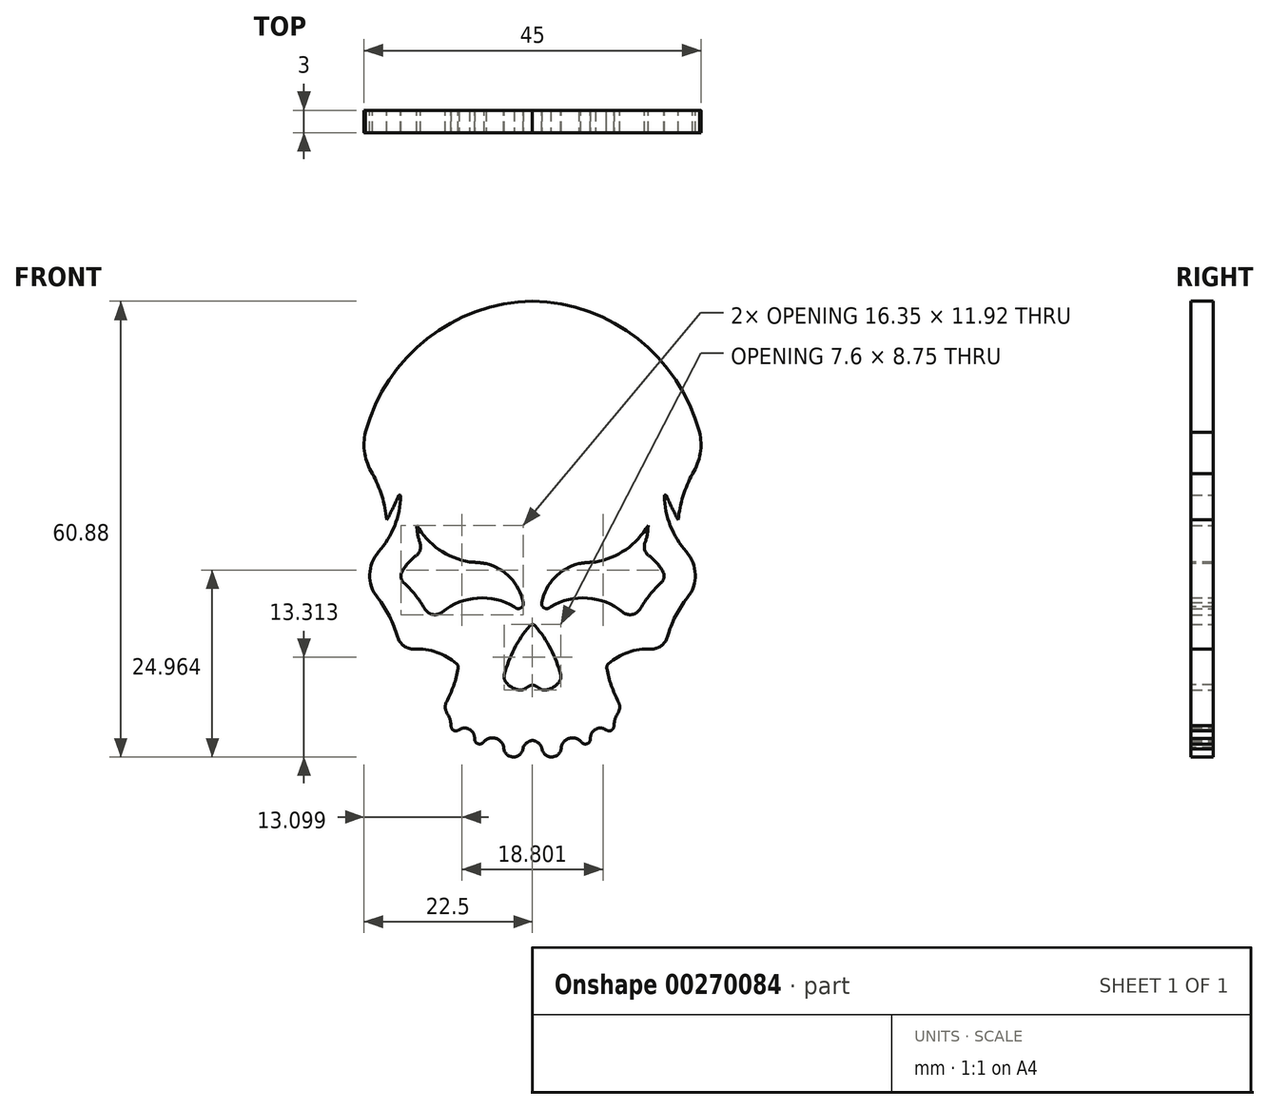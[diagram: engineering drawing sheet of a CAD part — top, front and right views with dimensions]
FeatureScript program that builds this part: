
annotation { "Feature Type Name" : "Feature", "Feature Type Description" : "" }
export const myFeature = defineFeature(function(context is Context, id is Id, definition is map)
    precondition{}
    {
        {
            var Q0;
            Q0=qCreatedBy(makeId("Front.planeOp"),FACE);
            var sketch = newSketch(context, id + "F0", { "sketchPlane" : qUnion([Q0])});
            skArc(sketch, "E0", {"start": v(-2.42, -10.37) * mm, "mid": v(-1.6, -10.56) * mm, "end": v(-1.24, -9.8) * mm});
            skArc(sketch, "E1", {"start": v(-1.24, -9.8) * mm, "mid": v(-2.95, -6.49) * mm, "end": v(-6.18, -4.63) * mm});
            skArc(sketch, "E2", {"start": v(-6.18, -4.63) * mm, "mid": v(-7.29, -4.47) * mm, "end": v(-8.4, -4.39) * mm});
            skArc(sketch, "E3", {"start": v(-15.43, 0.48) * mm, "mid": v(-12.46, -2.74) * mm, "end": v(-8.4, -4.39) * mm});
            skArc(sketch, "E4", {"start": v(-15.43, 0.48) * mm, "mid": v(-15.34, -0.68) * mm, "end": v(-15.03, -1.8) * mm});
            skArc(sketch, "E5", {"start": v(-15.54, -3.56) * mm, "mid": v(-14.99, -2.77) * mm, "end": v(-15.03, -1.8) * mm});
            skArc(sketch, "E6", {"start": v(-15.54, -3.56) * mm, "mid": v(-16.6, -4.54) * mm, "end": v(-17.43, -5.72) * mm});
            skArc(sketch, "E7", {"start": v(-17.43, -5.72) * mm, "mid": v(-17.56, -6.46) * mm, "end": v(-17.2, -7.12) * mm});
            skArc(sketch, "E8", {"start": v(-14.4, -10.64) * mm, "mid": v(-15.68, -8.78) * mm, "end": v(-17.2, -7.12) * mm});
            skArc(sketch, "E9", {"start": v(-14.4, -10.64) * mm, "mid": v(-13.32, -11.4) * mm, "end": v(-12.03, -11.08) * mm});
            skArc(sketch, "E10", {"start": v(-2.42, -10.37) * mm, "mid": v(-7.34, -9.21) * mm, "end": v(-12.03, -11.08) * mm});
            skArc(sketch, "E11", {"start": v(0.37, -12.92) * mm, "mid": v(0.2, -12.8) * mm, "end": v(0, -12.75) * mm});
            skArc(sketch, "E12", {"start": v(0, -12.75) * mm, "mid": v(-0.2, -12.8) * mm, "end": v(-0.37, -12.92) * mm});
            skArc(sketch, "E13", {"start": v(-0.37, -12.92) * mm, "mid": v(-2.44, -16) * mm, "end": v(-3.77, -19.48) * mm});
            skArc(sketch, "E14", {"start": v(-3.77, -19.48) * mm, "mid": v(-3.79, -19.89) * mm, "end": v(-3.65, -20.27) * mm});
            skArc(sketch, "E15", {"start": v(-3.65, -20.27) * mm, "mid": v(-2.9, -21.07) * mm, "end": v(-1.87, -21.48) * mm});
            skArc(sketch, "E16", {"start": v(-1.87, -21.48) * mm, "mid": v(-1.33, -21.46) * mm, "end": v(-0.85, -21.23) * mm});
            skArc(sketch, "E17", {"start": v(0, -20.8) * mm, "mid": v(-0.44, -20.97) * mm, "end": v(-0.85, -21.23) * mm});
            skArc(sketch, "E18", {"start": v(0.85, -21.23) * mm, "mid": v(0.44, -20.97) * mm, "end": v(0, -20.8) * mm});
            skArc(sketch, "E19", {"start": v(1.25, -29.2) * mm, "mid": v(0.75, -28.55) * mm, "end": v(0, -28.23) * mm});
            skArc(sketch, "E20", {"start": v(0, -28.23) * mm, "mid": v(-0.75, -28.55) * mm, "end": v(-1.25, -29.2) * mm});
            skArc(sketch, "E21", {"start": v(-3.82, -29.38) * mm, "mid": v(-2.46, -30.44) * mm, "end": v(-1.25, -29.2) * mm});
            skArc(sketch, "E22", {"start": v(-3.82, -29.38) * mm, "mid": v(-4.8, -27.99) * mm, "end": v(-6.46, -28.37) * mm});
            skArc(sketch, "E23", {"start": v(-7.74, -28) * mm, "mid": v(-7.25, -28.69) * mm, "end": v(-6.46, -28.37) * mm});
            skArc(sketch, "E24", {"start": v(-7.74, -28) * mm, "mid": v(-8.4, -26.76) * mm, "end": v(-9.8, -26.8) * mm});
            skArc(sketch, "E25", {"start": v(-10.87, -26.26) * mm, "mid": v(-10.5, -26.89) * mm, "end": v(-9.8, -26.8) * mm});
            skArc(sketch, "E26", {"start": v(-10.87, -26.26) * mm, "mid": v(-11.05, -25.37) * mm, "end": v(-11.43, -24.54) * mm});
            skArc(sketch, "E27", {"start": v(-11.48, -23.07) * mm, "mid": v(-11.65, -23.8) * mm, "end": v(-11.43, -24.54) * mm});
            skArc(sketch, "E28", {"start": v(-11.48, -23.07) * mm, "mid": v(-10.53, -20.9) * mm, "end": v(-9.92, -18.63) * mm});
            skArc(sketch, "E29", {"start": v(-9.92, -18.63) * mm, "mid": v(-9.94, -18.28) * mm, "end": v(-10.14, -17.98) * mm});
            skArc(sketch, "E30", {"start": v(-10.14, -17.98) * mm, "mid": v(-12.77, -16.46) * mm, "end": v(-15.78, -16.03) * mm});
            skArc(sketch, "E31", {"start": v(-18, -14.41) * mm, "mid": v(-17.18, -15.6) * mm, "end": v(-15.78, -16.03) * mm});
            skArc(sketch, "E32", {"start": v(-18, -14.41) * mm, "mid": v(-19.09, -11.65) * mm, "end": v(-20.7, -9.16) * mm});
            skArc(sketch, "E33", {"start": v(-20.54, -3.04) * mm, "mid": v(-21.73, -6.07) * mm, "end": v(-20.7, -9.16) * mm});
            skArc(sketch, "E34", {"start": v(-20.54, -3.04) * mm, "mid": v(-18.41, 0.42) * mm, "end": v(-17.6, 4.4) * mm});
            skArc(sketch, "E35", {"start": v(-17.6, 4.4) * mm, "mid": v(-17.7, 4.54) * mm, "end": v(-17.86, 4.46) * mm});
            skArc(sketch, "E36", {"start": v(-19.45, 1.22) * mm, "mid": v(-18.63, 2.83) * mm, "end": v(-17.86, 4.46) * mm});
            skArc(sketch, "E37", {"start": v(-19.45, 1.22) * mm, "mid": v(-20.11, 4.41) * mm, "end": v(-21.37, 7.4) * mm});
            skArc(sketch, "E38", {"start": v(-22.3, 12.95) * mm, "mid": v(-22.4, 10.09) * mm, "end": v(-21.37, 7.4) * mm});
            skArc(sketch, "E39", {"start": v(0, 30.44) * mm, "mid": v(-14.06, 25.41) * mm, "end": v(-22.3, 12.95) * mm});
            skArc(sketch, "E40.MirrorCS", {"start": v(17.6, 4.4) * mm, "mid": v(17.7, 4.54) * mm, "end": v(17.86, 4.46) * mm});
            skArc(sketch, "E41.MirrorCS", {"start": v(0, -12.75) * mm, "mid": v(0.2, -12.8) * mm, "end": v(0.37, -12.92) * mm});
            skArc(sketch, "E42.MirrorCS", {"start": v(-0.37, -12.92) * mm, "mid": v(-0.2, -12.8) * mm, "end": v(0, -12.75) * mm});
            skArc(sketch, "E43.MirrorCS", {"start": v(-0.85, -21.23) * mm, "mid": v(-0.44, -20.97) * mm, "end": v(0, -20.8) * mm});
            skArc(sketch, "E44.MirrorCS", {"start": v(0, -20.8) * mm, "mid": v(0.44, -20.97) * mm, "end": v(0.85, -21.23) * mm});
            skArc(sketch, "E45.MirrorCS", {"start": v(1.87, -21.48) * mm, "mid": v(1.33, -21.46) * mm, "end": v(0.85, -21.23) * mm});
            skArc(sketch, "E46.MirrorCS", {"start": v(-1.25, -29.2) * mm, "mid": v(-0.75, -28.55) * mm, "end": v(0, -28.23) * mm});
            skArc(sketch, "E47.MirrorCS", {"start": v(0, -28.23) * mm, "mid": v(0.75, -28.55) * mm, "end": v(1.25, -29.2) * mm});
            skArc(sketch, "E48.MirrorCS", {"start": v(10.87, -26.26) * mm, "mid": v(10.5, -26.89) * mm, "end": v(9.8, -26.8) * mm});
            skArc(sketch, "E49.MirrorCS", {"start": v(7.74, -28) * mm, "mid": v(7.25, -28.69) * mm, "end": v(6.46, -28.37) * mm});
            skArc(sketch, "E50.MirrorCS", {"start": v(14.4, -10.64) * mm, "mid": v(13.32, -11.4) * mm, "end": v(12.03, -11.08) * mm});
            skArc(sketch, "E51.MirrorCS", {"start": v(19.45, 1.22) * mm, "mid": v(18.63, 2.83) * mm, "end": v(17.86, 4.46) * mm});
            skArc(sketch, "E52.MirrorCS", {"start": v(9.92, -18.63) * mm, "mid": v(9.94, -18.28) * mm, "end": v(10.14, -17.98) * mm});
            skArc(sketch, "E53.MirrorCS", {"start": v(17.43, -5.72) * mm, "mid": v(17.56, -6.46) * mm, "end": v(17.2, -7.12) * mm});
            skArc(sketch, "E54.MirrorCS", {"start": v(15.54, -3.56) * mm, "mid": v(16.6, -4.54) * mm, "end": v(17.43, -5.72) * mm});
            skArc(sketch, "E55.MirrorCS", {"start": v(15.54, -3.56) * mm, "mid": v(14.99, -2.77) * mm, "end": v(15.03, -1.8) * mm});
            skArc(sketch, "E56.MirrorCS", {"start": v(15.43, 0.48) * mm, "mid": v(15.34, -0.68) * mm, "end": v(15.03, -1.8) * mm});
            skArc(sketch, "E57.MirrorCS", {"start": v(11.48, -23.07) * mm, "mid": v(11.65, -23.8) * mm, "end": v(11.43, -24.54) * mm});
            skArc(sketch, "E58.MirrorCS", {"start": v(6.18, -4.63) * mm, "mid": v(7.29, -4.47) * mm, "end": v(8.4, -4.39) * mm});
            skArc(sketch, "E59.MirrorCS", {"start": v(2.42, -10.37) * mm, "mid": v(1.6, -10.56) * mm, "end": v(1.24, -9.8) * mm});
            skArc(sketch, "E60.MirrorCS", {"start": v(3.65, -20.27) * mm, "mid": v(2.9, -21.07) * mm, "end": v(1.87, -21.48) * mm});
            skArc(sketch, "E61.MirrorCS", {"start": v(3.77, -19.48) * mm, "mid": v(3.79, -19.89) * mm, "end": v(3.65, -20.27) * mm});
            skArc(sketch, "E62.MirrorCS", {"start": v(18, -14.41) * mm, "mid": v(17.18, -15.6) * mm, "end": v(15.78, -16.03) * mm});
            skArc(sketch, "E63.MirrorCS", {"start": v(3.82, -29.38) * mm, "mid": v(4.8, -27.99) * mm, "end": v(6.46, -28.37) * mm});
            skArc(sketch, "E64.MirrorCS", {"start": v(3.82, -29.38) * mm, "mid": v(2.46, -30.44) * mm, "end": v(1.25, -29.2) * mm});
            skArc(sketch, "E65.MirrorCS", {"start": v(10.87, -26.26) * mm, "mid": v(11.05, -25.37) * mm, "end": v(11.43, -24.54) * mm});
            skArc(sketch, "E66.MirrorCS", {"start": v(7.74, -28) * mm, "mid": v(8.4, -26.76) * mm, "end": v(9.8, -26.8) * mm});
            skArc(sketch, "E67.MirrorCS", {"start": v(18, -14.41) * mm, "mid": v(19.09, -11.65) * mm, "end": v(20.7, -9.16) * mm});
            skArc(sketch, "E68.MirrorCS", {"start": v(0, 30.44) * mm, "mid": v(14.06, 25.41) * mm, "end": v(22.3, 12.95) * mm});
            skArc(sketch, "E69.MirrorCS", {"start": v(20.54, -3.04) * mm, "mid": v(21.73, -6.07) * mm, "end": v(20.7, -9.16) * mm});
            skArc(sketch, "E70.MirrorCS", {"start": v(2.42, -10.37) * mm, "mid": v(7.34, -9.21) * mm, "end": v(12.03, -11.08) * mm});
            skArc(sketch, "E71.MirrorCS", {"start": v(14.4, -10.64) * mm, "mid": v(15.68, -8.78) * mm, "end": v(17.2, -7.12) * mm});
            skArc(sketch, "E72.MirrorCS", {"start": v(20.54, -3.04) * mm, "mid": v(18.41, 0.42) * mm, "end": v(17.6, 4.4) * mm});
            skArc(sketch, "E73.MirrorCS", {"start": v(15.43, 0.48) * mm, "mid": v(12.46, -2.74) * mm, "end": v(8.4, -4.39) * mm});
            skArc(sketch, "E74.MirrorCS", {"start": v(1.24, -9.8) * mm, "mid": v(2.95, -6.49) * mm, "end": v(6.18, -4.63) * mm});
            skArc(sketch, "E75.MirrorCS", {"start": v(0.37, -12.92) * mm, "mid": v(2.44, -16) * mm, "end": v(3.77, -19.48) * mm});
            skArc(sketch, "E76.MirrorCS", {"start": v(22.3, 12.95) * mm, "mid": v(22.4, 10.09) * mm, "end": v(21.37, 7.4) * mm});
            skArc(sketch, "E77.MirrorCS", {"start": v(10.14, -17.98) * mm, "mid": v(12.77, -16.46) * mm, "end": v(15.78, -16.03) * mm});
            skArc(sketch, "E78.MirrorCS", {"start": v(11.48, -23.07) * mm, "mid": v(10.53, -20.9) * mm, "end": v(9.92, -18.63) * mm});
            skArc(sketch, "E79.MirrorCS", {"start": v(19.45, 1.22) * mm, "mid": v(20.11, 4.41) * mm, "end": v(21.37, 7.4) * mm});
            skSolve(sketch);
        }
        {
            var Q0;
            Q0 = qSketchRegion(id + "F0", true);
            extrude(context, id + "F1", {"entities" : qUnion([Q0]), "depth" : 3 * mm});
        }
    });
